# Revit family: Overhead_Door-CHI-Planks-Stylelite
name_source: partatom
category: Specialty Equipment
units: mm (PartAtom-declared; Revit-internal decimal feet)

## family parameters
Always vertical = Yes
Cut with Voids When Loaded = No
Host = Wall
OmniClass Number = 23.30.10.21
OmniClass Title = Special Function Doors
Part Type = Normal
Room Calculation Point = No
Round Connector Dimension = Use Diameter
Shared = No

## types (16) — shared parameters
Air Infiltration = 0.1
Assembly Code = B2050.10
C Door Bottom Offset = 0.03'
C Model = 4
C OFG = 0.00'
C Panel Size = 2
C Side Rail Radius = 1.25'
Certified Windload = Yes
Construction Type = Glass garage doors
DASMA Thermal Verification Program = Yes
Default Elevation = 0.00'
Description = Wood-Look Garage Doors
Fire Rating = Contact Manufacturer for More Information
Flame Spread = 15
Glass Finish = Glass - C.H.I Overhead Doors - Frosted
IECC Compliant = Yes
Impact = Yes
Keynote = 08 30 00
Load Classification = Other
Long Panel = Yes
Manufacturer = C.H.I. Overhead Doors
Manufacturer Fax Number = 800-738-5006
Material Disclaimer = Accents Woodtones, when ordered, contain non-repeating patterns. Color discrepancies may appear differently on desktop displays. Contact Manufacturer for Availability of Finishes per Model
Model = 2348
Number of Phases = 1
Number of Poles = 1
Product Documentation Link = https://www.chiohd.com
Product Page URL = https://www.chiohd.com
R-Value = 17.54
Short Panel = No
Steel Gauge = 27
Thickness = 0.17'
U Factor = 0.19
URL = https://www.chiohd.com
Version = 2021-v1.a
Voltage = 115 V

## per-type parameters (varying)
| type | Panel Finish |
| 2348 - Almond | Metal - Powder Coat - C.H.I Overhead Doors - Almond |
| 2348 - Black | Metal - Powder Coat - C.H.I Overhead Doors - Black |
| 2348 - Bronze | Metal - Powder Coat - C.H.I Overhead Doors - Bronze |
| 2348 - Brown | Metal - Powder Coat - C.H.I Overhead Doors - Brown |
| 2348 - Desert Tan | Metal - Powder Coat - C.H.I Overhead Doors - Desert Tan |
| 2348 - Graphite | Metal - Powder Coat - C.H.I Overhead Doors - Graphite |
| 2348 - Gray | Metal - Powder Coat - C.H.I Overhead Doors - Gray |
| 2348 - Sandstone | Metal - Powder Coat - C.H.I Overhead Doors - Sandstone |
| 2348 - White | Metal - Powder Coat - C.H.I Overhead Doors - White |
| 2348 - Carbon Oak | Wood - Accents Woodtones - C.H.I Overhead Doors - Plank - Carbon Oak |
| 2348 - Cedar | Wood - Accents Woodtones - C.H.I Overhead Doors - Plank - Cedar |
| 2348 - Dark Oak | Wood - Accents Woodtones - C.H.I Overhead Doors - Plank - Dark Oak |
| 2348 - Driftwood | Wood - Accents Woodtones - C.H.I Overhead Doors - Plank - Driftwood |
| 2348 - Mahogany | Wood - Accents Woodtones - C.H.I Overhead Doors - Plank - Mahogany |
| 2348 - Natural Oak | Wood - Accents Woodtones - C.H.I Overhead Doors - Plank - Natural Oak |
| 2348 - Walnut | Wood - Accents Woodtones - C.H.I Overhead Doors - Plank - Walnut |

## geometry (parser evidence)
native form markers: Sweep x44
no freeform markers — native parametric forms only
